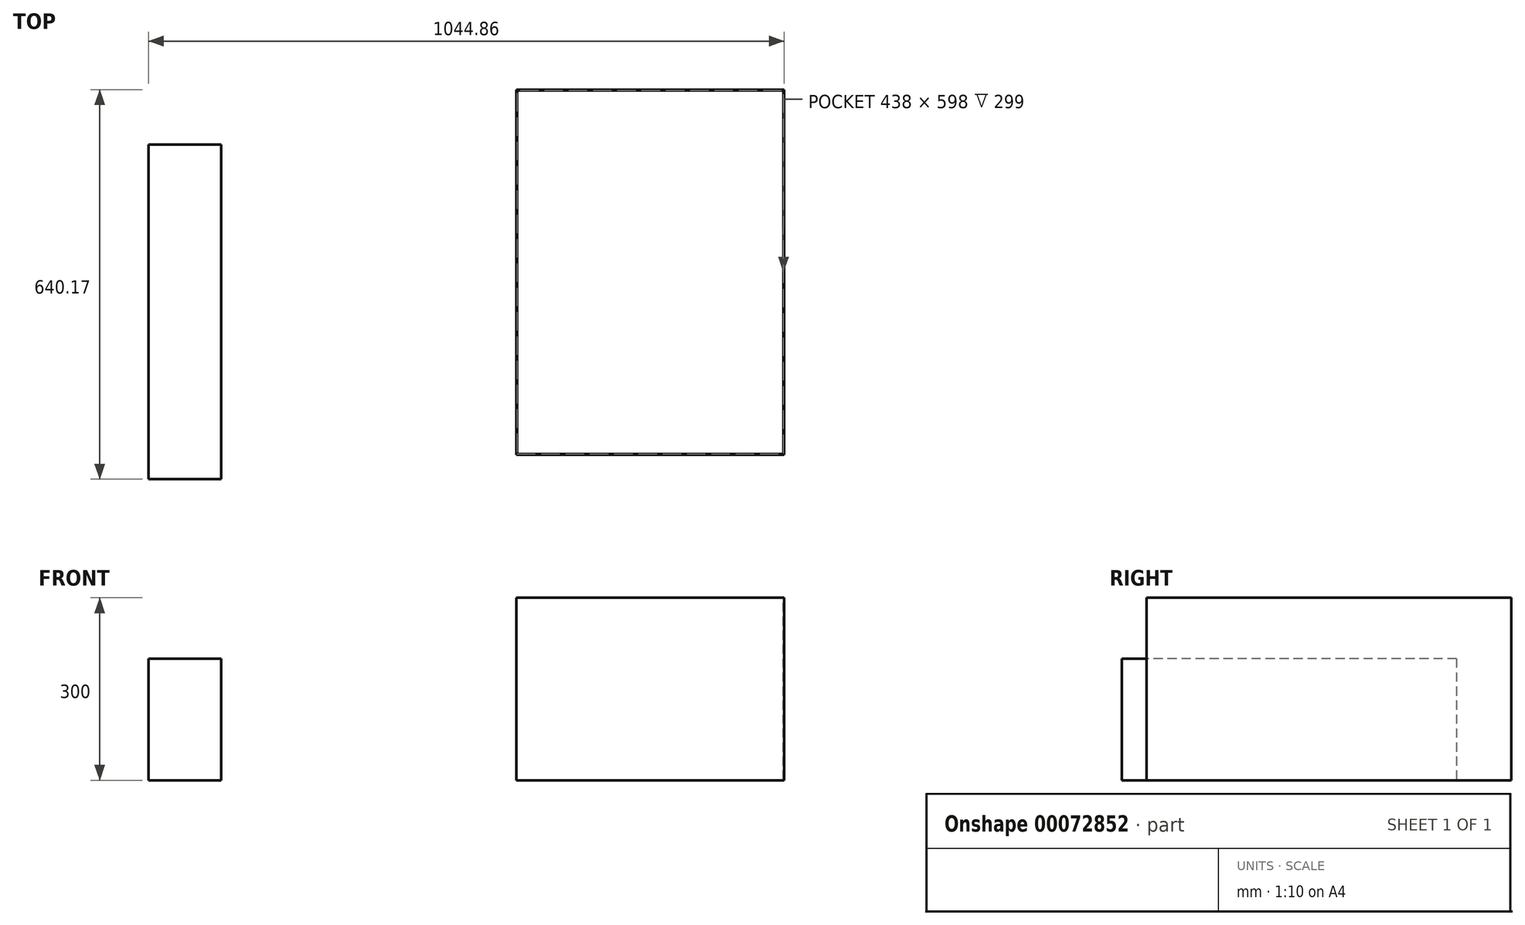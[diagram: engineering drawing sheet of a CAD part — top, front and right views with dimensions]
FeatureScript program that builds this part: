
annotation { "Feature Type Name" : "Feature", "Feature Type Description" : "" }
export const myFeature = defineFeature(function(context is Context, id is Id, definition is map)
    precondition{}
    {
        {
            var Q0;
            Q0=qCreatedBy(makeId("Top.planeOp"),FACE);
            var sketch = newSketch(context, id + "F0", { "sketchPlane" : qUnion([Q0])});
            skLineSegment(sketch, "E0.bottom", {"start": v(-229.75, 356.7) * mm, "end": v(210.25, 356.7) * mm});
            skLineSegment(sketch, "E0.top", {"start": v(-229.75, -243.3) * mm, "end": v(210.25, -243.3) * mm});
            skLineSegment(sketch, "E0.left", {"start": v(-229.75, 356.7) * mm, "end": v(-229.75, -243.3) * mm});
            skLineSegment(sketch, "E0.right", {"start": v(210.25, 356.7) * mm, "end": v(210.25, -243.3) * mm});
            skSolve(sketch);
        }
        {
            var Q0;
            Q0 = qSketchRegion(id + "F0", true);
            extrude(context, id + "F1", {"entities" : qUnion([Q0]), "depth" : 300 * mm});
        }
        {
            var Q0;
            Q0=makeQuery(id+"F1.opExtrude","CAP_FACE",FACE,{"disambiguationData":[OSD([sQuery(id+"F0.wireOp",EDGE,"E0.bottom"),sQuery(id+"F0.wireOp",EDGE,"E0.top"),sQuery(id+"F0.wireOp",EDGE,"E0.left"),sQuery(id+"F0.wireOp",EDGE,"E0.right")])],"isStart":false});
            var sketch = newSketch(context, id + "F2", { "sketchPlane" : qUnion([Q0])});
            skLineSegment(sketch, "E1.bottom", {"start": v(-228.75, -242.3) * mm, "end": v(209.25, -242.3) * mm});
            skLineSegment(sketch, "E1.top", {"start": v(-228.75, 355.7) * mm, "end": v(209.25, 355.7) * mm});
            skLineSegment(sketch, "E1.left", {"start": v(-228.75, -242.3) * mm, "end": v(-228.75, 355.7) * mm});
            skLineSegment(sketch, "E1.right", {"start": v(209.25, -242.3) * mm, "end": v(209.25, 355.7) * mm});
            skSolve(sketch);
        }
        {
            var Q0;
            Q0 = qSketchRegion(id + "F2", true);
            extrude(context, id + "F3", {"entities" : qUnion([Q0]), "operationType" : NewBodyOperationType.REMOVE, "oppositeDirection" : true, "depth" : 299 * mm});
        }
        {
            var Q0;
            Q0=qCreatedBy(makeId("Top.planeOp"),FACE);
            var sketch = newSketch(context, id + "F4", { "sketchPlane" : qUnion([Q0])});
            skLineSegment(sketch, "E2.bottom", {"start": v(-834.6, 266.53) * mm, "end": v(-714.6, 266.53) * mm});
            skLineSegment(sketch, "E2.top", {"start": v(-834.6, -283.47) * mm, "end": v(-714.6, -283.47) * mm});
            skLineSegment(sketch, "E2.left", {"start": v(-834.6, 266.53) * mm, "end": v(-834.6, -283.47) * mm});
            skLineSegment(sketch, "E2.right", {"start": v(-714.6, 266.53) * mm, "end": v(-714.6, -283.47) * mm});
            skSolve(sketch);
        }
        {
            var Q0;
            Q0 = qSketchRegion(id + "F4", true);
            extrude(context, id + "F5", {"entities" : qUnion([Q0]), "depth" : 200 * mm});
        }
    });
